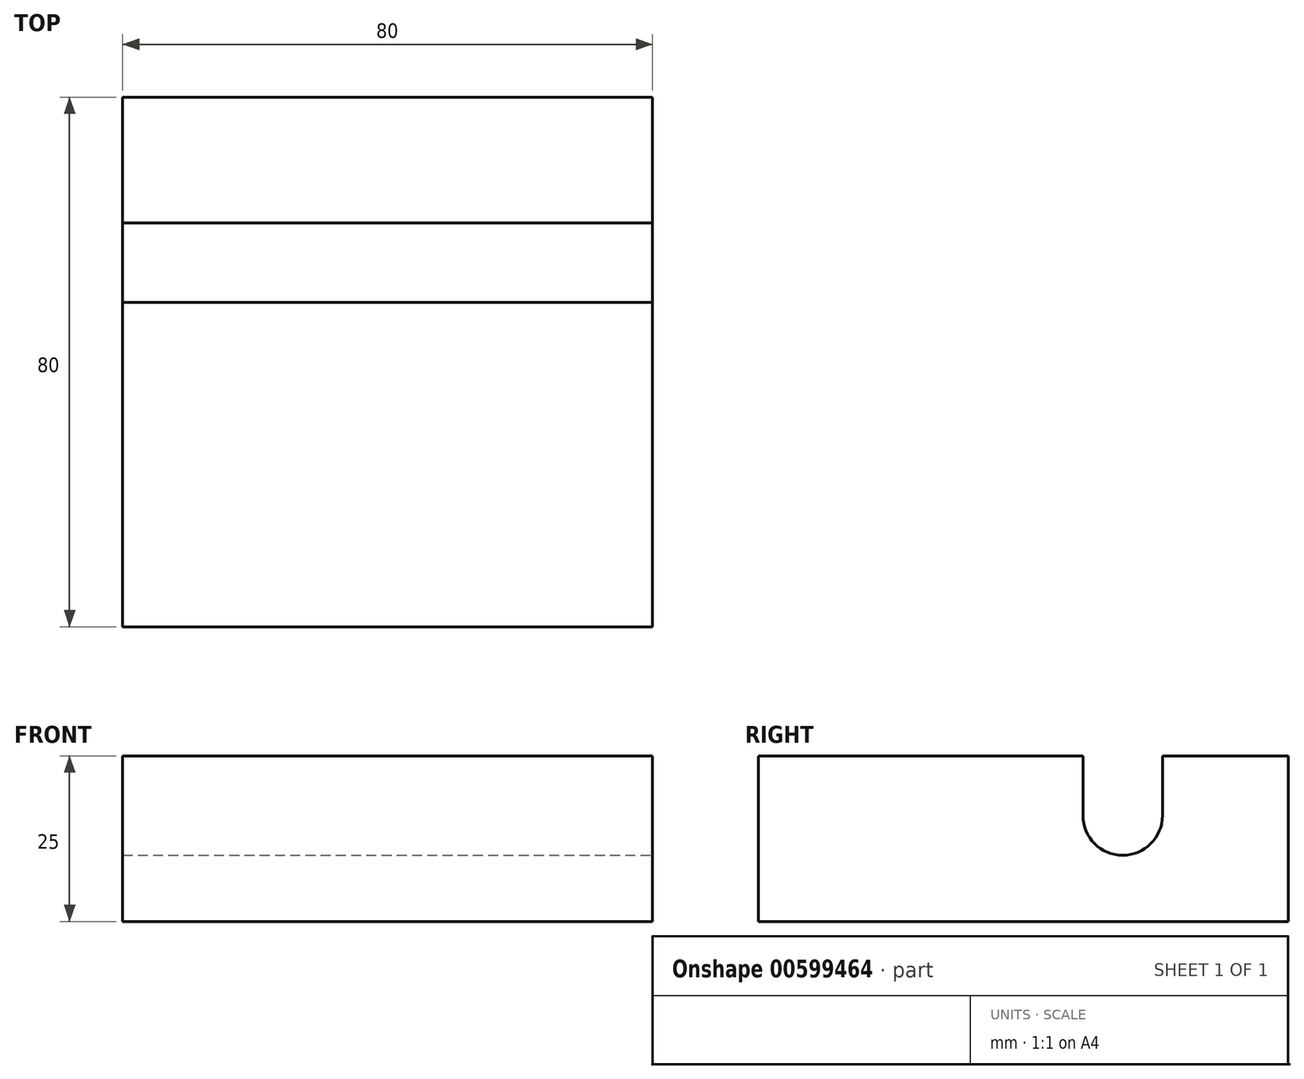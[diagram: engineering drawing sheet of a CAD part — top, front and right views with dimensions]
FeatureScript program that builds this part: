
annotation { "Feature Type Name" : "Feature", "Feature Type Description" : "" }
export const myFeature = defineFeature(function(context is Context, id is Id, definition is map)
    precondition{}
    {
        {
            var Q0;
            Q0=qCreatedBy(makeId("Top.planeOp"),FACE);
            var sketch = newSketch(context, id + "F0", { "sketchPlane" : qUnion([Q0])});
            skLineSegment(sketch, "E0.bottom", {"start": v(-40, 40) * mm, "end": v(40, 40) * mm});
            skLineSegment(sketch, "E0.top", {"start": v(-40, -40) * mm, "end": v(40, -40) * mm});
            skLineSegment(sketch, "E0.left", {"start": v(-40, 40) * mm, "end": v(-40, -40) * mm});
            skLineSegment(sketch, "E0.right", {"start": v(40, 40) * mm, "end": v(40, -40) * mm});
            skPoint(sketch, "E0.middle", {"position": v(0, 0) * mm});
            skSolve(sketch);
        }
        {
            var Q0;
            Q0 = qSketchRegion(id + "F0", true);
            extrude(context, id + "F1", {"entities" : qUnion([Q0]), "depth" : 25 * mm, "offsetDistance" : 25 * mm});
        }
        {
            var Q0;
            Q0=makeQuery(id+"F1.opExtrude","CAP_FACE",FACE,{"disambiguationData":[OSD([sQuery(id+"F0.wireOp",EDGE,"E0.bottom"),sQuery(id+"F0.wireOp",EDGE,"E0.top"),sQuery(id+"F0.wireOp",EDGE,"E0.left"),sQuery(id+"F0.wireOp",EDGE,"E0.right")])],"isStart":false});
            var sketch = newSketch(context, id + "F2", { "sketchPlane" : qUnion([Q0])});
            skLineSegment(sketch, "E1.bottom", {"start": v(-40, 21) * mm, "end": v(40, 21) * mm});
            skLineSegment(sketch, "E1.top", {"start": v(-40, 9) * mm, "end": v(40, 9) * mm});
            skLineSegment(sketch, "E1.left", {"start": v(-40, 21) * mm, "end": v(-40, 9) * mm});
            skLineSegment(sketch, "E1.right", {"start": v(40, 21) * mm, "end": v(40, 9) * mm});
            skPoint(sketch, "E1.middle", {"position": v(0, 15) * mm});
            skSolve(sketch);
        }
        {
            var Q0;
            Q0 = qSketchRegion(id + "F2", true);
            extrude(context, id + "F3", {"entities" : qUnion([Q0]), "operationType" : NewBodyOperationType.REMOVE, "oppositeDirection" : true, "depth" : 15 * mm, "offsetDistance" : 25 * mm});
        }
        {
            var Q0;
            Q0=makeQuery(id+"F3.boolean.opBoolean","COPY",EDGE,{"derivedFrom":makeQuery(id+"F3.opExtrude","CAP_EDGE",EDGE,{"disambiguationData":[OSD([sQuery(id+"F2.wireOp",EDGE,"E1.top")])],"isStart":false})});
            var Q1;
            Q1=makeQuery(id+"F3.boolean.opBoolean","COPY",EDGE,{"derivedFrom":makeQuery(id+"F3.opExtrude","CAP_EDGE",EDGE,{"disambiguationData":[OSD([sQuery(id+"F2.wireOp",EDGE,"E1.bottom")])],"isStart":false})});
            fillet(context, id + "F4", {"entities" : qUnion([Q0, Q1]), "radius" : 6 * mm, "tangentPropagation" : true, "allowEdgeOverflow" : false});
        }
    });
